# Revit family: 306_588758854409416bb3ba4b6bac1a4a
name_source: partatom
category: Pipe Accessories
units: mm (PartAtom-declared; Revit-internal decimal feet)

## family parameters
Always vertical = Yes
Cut with Voids When Loaded = No
Part Type = Valve - Breaks Into
Round Connector Dimension = Use Diameter
Shared = No
Work Plane-Based = No

## types (5) — shared parameters
Description = 3-way Change-over valve VRG231, PN10 internal thread
L2D_Min = 3048 mm
MC = No
Manufacturer = ESBE
QmdConnectorList = 301;D;302;D
URL = http://www.esbe.eu
X5 = 2 mm  [stored 0.00656168 ft]
Z6 = 2 mm  [stored 0.00656168 ft]
magiPartTypeId = 306
magiProductFamilyId = 588758854409416bb3ba4b6bac1a4a

## per-type parameters (varying)
| type | A | C | CenSd_NR_6 | D | D1 | L2D | NR | W2D | X1 | X2 | X2__ve | X6 | Y0 | Y2 | Y3 | Y6 | Y7 | Y9 | Z5 | Z5__ve | Z7 | Z7__ve | magiProductId |
| VRG231 20-6.3 RP 3/4 | 36 mm  [stored 0.11811 ft] | 32 mm  [stored 0.104987 ft] | 11 mm  [stored 0.0360892 ft] | 20 mm | 50 mm | 72 mm | 13 mm  [stored 0.0426509 ft] | 20 mm  [stored 0.0656168 ft] | 36 mm  [stored 0.11811 ft] | 8 mm  [stored 0.0262467 ft] | -8 mm | 52 mm | 10 mm  [stored 0.0328084 ft] | 11 mm  [stored 0.0360892 ft] | 20 mm  [stored 0.0656168 ft] | 19 mm | 17 mm | 16 mm  [stored 0.0524934 ft] | 8 mm  [stored 0.0262467 ft] | -8 mm | 26 mm  [stored 0.0853018 ft] | -26 mm | 0ca3b6afe6e140c7a460330fec616f |
| VRG231 50-40 RP 2 | 60 mm | 46 mm | 28 mm | 50 mm | 64 mm | 120 mm | 33 mm | 50 mm | 60 mm | 13 mm  [stored 0.0426509 ft] | -13 mm  [stored -0.0426509 ft] | 90 mm | 25 mm  [stored 0.082021 ft] | 28 mm | 34 mm  [stored 0.111549 ft] | 33 mm | 31 mm | 30 mm  [stored 0.0984252 ft] | 13 mm  [stored 0.0426509 ft] | -13 mm  [stored -0.0426509 ft] | 45 mm | -45 mm | c704198724d246fa9d4d16add5659d |
| VRG231 40-30 RP 1½ | 53 mm | 44 mm | 23 mm | 40 mm | 60 mm | 106 mm | 26 mm  [stored 0.0853018 ft] | 40 mm | 53 mm | 12 mm  [stored 0.0393701 ft] | -12 mm | 79 mm | 20 mm  [stored 0.0656168 ft] | 22 mm  [stored 0.0721785 ft] | 30 mm  [stored 0.0984252 ft] | 29 mm | 27 mm | 26 mm  [stored 0.0853018 ft] | 12 mm  [stored 0.0393701 ft] | -12 mm | 39 mm | -39 mm | 92074dc7ee6d423cbe02d6a50cacb5 |
| VRG231 32-16 RP 1¼ | 47 mm | 37 mm  [stored 0.121391 ft] | 18 mm  [stored 0.0590551 ft] | 32 mm | 55 mm | 94 mm | 21 mm | 32 mm  [stored 0.104987 ft] | 47 mm | 10 mm  [stored 0.0328084 ft] | -10 mm  [stored -0.0328084 ft] | 69 mm | 16 mm  [stored 0.0524934 ft] | 18 mm  [stored 0.0590551 ft] | 26 mm  [stored 0.0853018 ft] | 25 mm  [stored 0.082021 ft] | 23 mm | 22 mm  [stored 0.0721785 ft] | 10 mm  [stored 0.0328084 ft] | -10 mm  [stored -0.0328084 ft] | 35 mm | -35 mm | b16349320b1c4727a2fd37b9191fb9 |
| VRG231 25-10 RP 1 | 41 mm | 34 mm  [stored 0.111549 ft] | 14 mm  [stored 0.0459318 ft] | 25 mm | 52 mm | 82 mm | 16 mm  [stored 0.0524934 ft] | 25 mm  [stored 0.082021 ft] | 41 mm | 9 mm  [stored 0.0295276 ft] | -9 mm | 60 mm | 13 mm  [stored 0.0426509 ft] | 14 mm  [stored 0.0459318 ft] | 22 mm  [stored 0.0721785 ft] | 21 mm | 20 mm  [stored 0.0656168 ft] | 19 mm | 9 mm  [stored 0.0295276 ft] | -9 mm | 30 mm  [stored 0.0984252 ft] | -30 mm | b6b34b94a2cd45a9b710083a2134bc |

note: column(s) folded — value = type name in every type: magiProductCode

note: [stored X ft] marks values corroborated as IEEE doubles in the binary element streams (Revit-internal decimal feet)

## geometry (parser evidence)
native form markers: Sweep x1
no freeform markers — native parametric forms only
